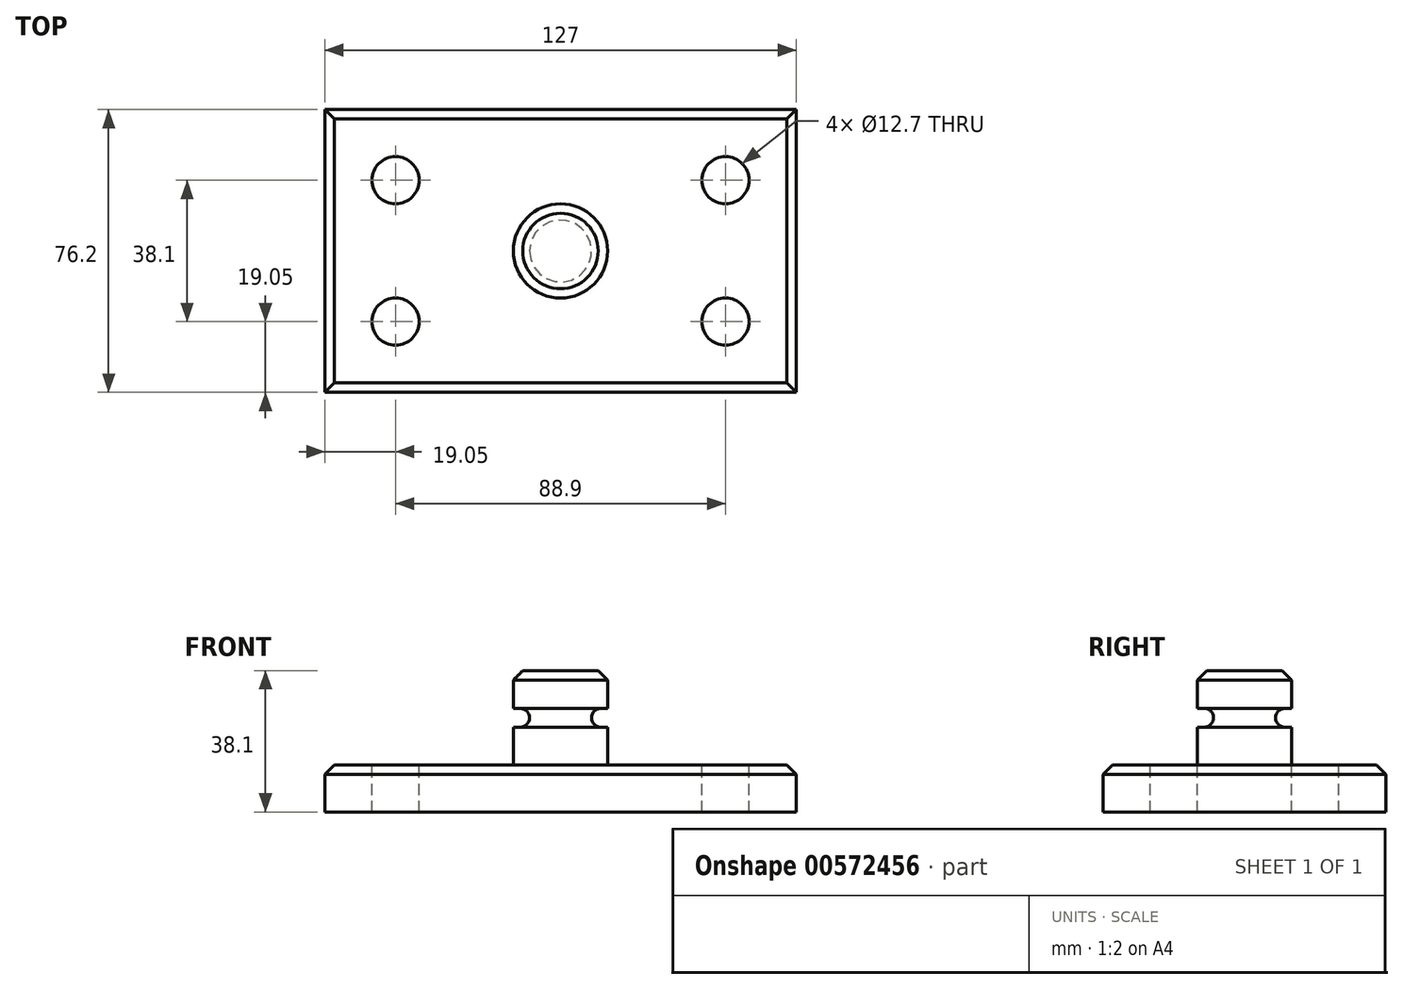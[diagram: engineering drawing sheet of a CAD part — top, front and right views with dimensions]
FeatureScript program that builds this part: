
annotation { "Feature Type Name" : "Feature", "Feature Type Description" : "" }
export const myFeature = defineFeature(function(context is Context, id is Id, definition is map)
    precondition{}
    {
        {
            var Q0;
            Q0=qCreatedBy(makeId("Top.planeOp"),FACE);
            var sketch = newSketch(context, id + "F0", { "sketchPlane" : qUnion([Q0])});
            skLineSegment(sketch, "E0.bottom", {"start": v(63.5, 38.1) * mm, "end": v(-63.5, 38.1) * mm});
            skLineSegment(sketch, "E0.top", {"start": v(63.5, -38.1) * mm, "end": v(-63.5, -38.1) * mm});
            skLineSegment(sketch, "E0.left", {"start": v(63.5, 38.1) * mm, "end": v(63.5, -38.1) * mm});
            skLineSegment(sketch, "E0.right", {"start": v(-63.5, 38.1) * mm, "end": v(-63.5, -38.1) * mm});
            skPoint(sketch, "E0.middle", {"position": v(0, 0) * mm});
            skSolve(sketch);
        }
        {
            var Q0;
            Q0=makeQuery(id+"F0.imprint","IMPRINT",FACE,{"disambiguationData":[TD([[makeQuery(id+"F0.imprint","IMPRINT",EDGE,{"derivedFrom":sQuery(id+"F0.wireOp",EDGE,"E0.bottom")}),1.0]])]});
            extrude(context, id + "F1", {"entities" : qUnion([Q0]), "depth" : 12.7 * mm, "offsetDistance" : 25.4 * mm});
        }
        {
            var Q0;
            Q0=makeQuery(id+"F1.opExtrude","CAP_FACE",FACE,{"disambiguationData":[OSD([sQuery(id+"F0.wireOp",EDGE,"E0.bottom"),sQuery(id+"F0.wireOp",EDGE,"E0.top"),sQuery(id+"F0.wireOp",EDGE,"E0.left"),sQuery(id+"F0.wireOp",EDGE,"E0.right")])],"isStart":false});
            var sketch = newSketch(context, id + "F2", { "sketchPlane" : qUnion([Q0])});
            skCircle(sketch, "E1", {"center": v(-44.45, -19.05) * mm, "radius": 6.35 * mm});
            skCircle(sketch, "E2", {"center": v(-44.45, 19.05) * mm, "radius": 6.35 * mm});
            skCircle(sketch, "E3", {"center": v(44.45, 19.05) * mm, "radius": 6.35 * mm});
            skCircle(sketch, "E4", {"center": v(44.45, -19.05) * mm, "radius": 6.35 * mm});
            skSolve(sketch);
        }
        {
            var Q0;
            Q0=makeQuery(id+"F2.imprint","IMPRINT",FACE,{"disambiguationData":[TD([[makeQuery(id+"F2.imprint","IMPRINT",EDGE,{"derivedFrom":sQuery(id+"F2.wireOp",EDGE,"E2")}),1.0]])]});
            var Q1;
            Q1=makeQuery(id+"F2.imprint","IMPRINT",FACE,{"disambiguationData":[TD([[makeQuery(id+"F2.imprint","IMPRINT",EDGE,{"derivedFrom":sQuery(id+"F2.wireOp",EDGE,"E3")}),1.0]])]});
            var Q2;
            Q2=makeQuery(id+"F2.imprint","IMPRINT",FACE,{"disambiguationData":[TD([[makeQuery(id+"F2.imprint","IMPRINT",EDGE,{"derivedFrom":sQuery(id+"F2.wireOp",EDGE,"E4")}),1.0]])]});
            var Q3;
            Q3=makeQuery(id+"F2.imprint","IMPRINT",FACE,{"disambiguationData":[TD([[makeQuery(id+"F2.imprint","IMPRINT",EDGE,{"derivedFrom":sQuery(id+"F2.wireOp",EDGE,"E1")}),1.0]])]});
            extrude(context, id + "F3", {"entities" : qUnion([Q0, Q1, Q2, Q3]), "operationType" : NewBodyOperationType.REMOVE, "endBound" : BoundingType.THROUGH_ALL, "oppositeDirection" : true, "depth" : 25.4 * mm, "offsetDistance" : 25.4 * mm});
        }
        {
            var Q0;
            Q0=makeQuery(id+"F1.opExtrude","CAP_EDGE",EDGE,{"disambiguationData":[OSD([sQuery(id+"F0.wireOp",EDGE,"E0.right")])],"isStart":false});
            var Q1;
            Q1=makeQuery(id+"F1.opExtrude","CAP_EDGE",EDGE,{"disambiguationData":[OSD([sQuery(id+"F0.wireOp",EDGE,"E0.bottom")])],"isStart":false});
            var Q2;
            Q2=makeQuery(id+"F1.opExtrude","CAP_EDGE",EDGE,{"disambiguationData":[OSD([sQuery(id+"F0.wireOp",EDGE,"E0.top")])],"isStart":false});
            var Q3;
            Q3=makeQuery(id+"F1.opExtrude","CAP_EDGE",EDGE,{"disambiguationData":[OSD([sQuery(id+"F0.wireOp",EDGE,"E0.left")])],"isStart":false});
            chamfer(context, id + "F4", {"entities" : qUnion([Q0, Q1, Q2, Q3]), "width" : 2.54 * mm, "tangentPropagation" : true});
        }
        {
            var Q0;
            Q0=qCreatedBy(makeId("Front.planeOp"),FACE);
            var sketch = newSketch(context, id + "F5", { "sketchPlane" : qUnion([Q0])});
            skLineSegment(sketch, "E5.bottom", {"start": v(0, 12.7) * mm, "end": v(12.7, 12.7) * mm});
            skLineSegment(sketch, "E5.top", {"start": v(0, 38.1) * mm, "end": v(12.7, 38.1) * mm});
            skLineSegment(sketch, "E5.left", {"start": v(0, 12.7) * mm, "end": v(0, 38.1) * mm});
            skLineSegment(sketch, "E6", {"start": v(12.7, 38.1) * mm, "end": v(12.7, 27.94) * mm});
            skLineSegment(sketch, "E7", {"start": v(12.7, 27.94) * mm, "end": v(8.35, 27.94) * mm});
            skLineSegment(sketch, "E8", {"start": v(8.35, 27.94) * mm, "end": v(8.35, 22.86) * mm});
            skLineSegment(sketch, "E9", {"start": v(8.35, 22.86) * mm, "end": v(12.7, 22.86) * mm});
            skLineSegment(sketch, "E10", {"start": v(12.7, 22.86) * mm, "end": v(12.7, 12.7) * mm});
            skSolve(sketch);
        }
        {
            var Q0;
            Q0=makeQuery(id+"F5.imprint","IMPRINT",FACE,{"disambiguationData":[TD([[makeQuery(id+"F5.imprint","IMPRINT",EDGE,{"derivedFrom":sQuery(id+"F5.wireOp",EDGE,"E5.bottom")}),1.0]])]});
            var Q1;
            Q1=sQuery(id+"F5.wireOp",EDGE,"E5.left");
            revolve(context, id + "F6", {"operationType" : NewBodyOperationType.ADD, "entities" : qUnion([Q0]), "axis" : qUnion([Q1]), "revolveType" : RevolveType.FULL});
        }
        {
            var Q0;
            Q0=makeQuery(id+"F6.opRevolve","SWEPT_EDGE",EDGE,{"disambiguationData":[OSD([sQuery(id+"F5.wireOp",EDGE,"E5.bottom"),sQuery(id+"F5.wireOp",EDGE,"E10")])]});
            var Q1;
            Q1=makeQuery(id+"F6.opRevolve","SWEPT_EDGE",EDGE,{"disambiguationData":[OSD([sQuery(id+"F5.wireOp",EDGE,"E8"),sQuery(id+"F5.wireOp",EDGE,"E9")])]});
            var Q2;
            Q2=makeQuery(id+"F6.opRevolve","SWEPT_EDGE",EDGE,{"disambiguationData":[OSD([sQuery(id+"F5.wireOp",EDGE,"E7"),sQuery(id+"F5.wireOp",EDGE,"E8")])]});
            fillet(context, id + "F7", {"entities" : qUnion([Q0, Q1, Q2]), "radius" : 2.54 * mm, "tangentPropagation" : true, "allowEdgeOverflow" : false});
        }
        {
            var Q0;
            Q0=makeQuery(id+"F6.opRevolve","SWEPT_EDGE",EDGE,{"disambiguationData":[OSD([sQuery(id+"F5.wireOp",EDGE,"E5.top"),sQuery(id+"F5.wireOp",EDGE,"E6")])]});
            chamfer(context, id + "F8", {"entities" : qUnion([Q0]), "width" : 2.54 * mm, "tangentPropagation" : true});
        }
    });
